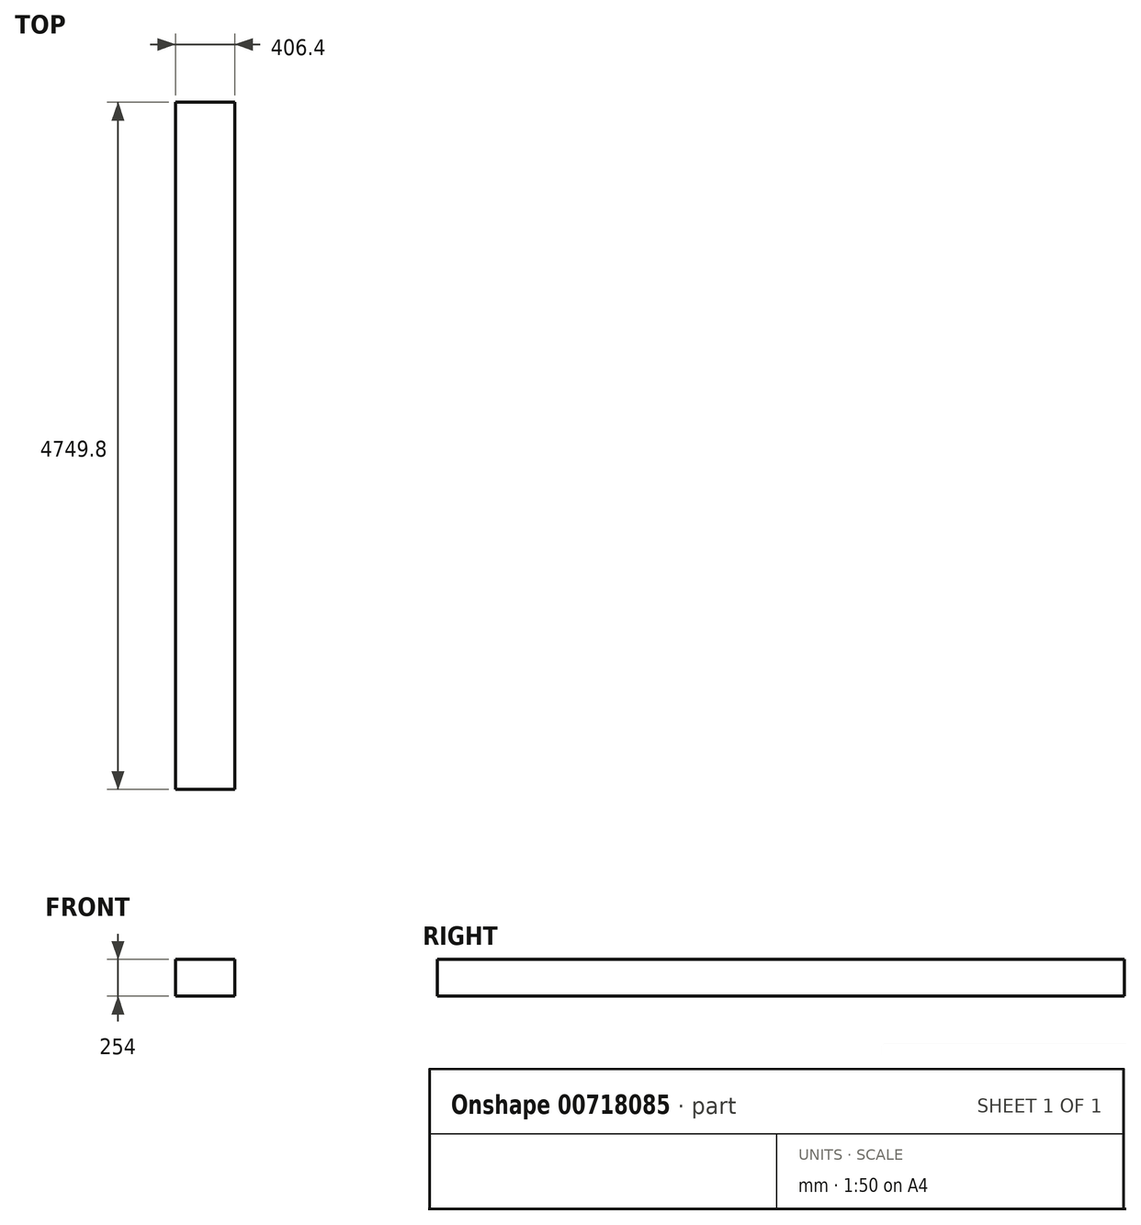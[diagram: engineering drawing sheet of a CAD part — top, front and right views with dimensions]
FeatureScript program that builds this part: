
annotation { "Feature Type Name" : "Feature", "Feature Type Description" : "" }
export const myFeature = defineFeature(function(context is Context, id is Id, definition is map)
    precondition{}
    {
        {
            var Q0;
            Q0=qCreatedBy(makeId("Front.planeOp"),FACE);
            var sketch = newSketch(context, id + "F0", { "sketchPlane" : qUnion([Q0])});
            skLineSegment(sketch, "E0.bottom", {"start": v(203.2, -127) * mm, "end": v(-203.2, -127) * mm});
            skLineSegment(sketch, "E0.top", {"start": v(203.2, 127) * mm, "end": v(-203.2, 127) * mm});
            skLineSegment(sketch, "E0.left", {"start": v(203.2, -127) * mm, "end": v(203.2, 127) * mm});
            skLineSegment(sketch, "E0.right", {"start": v(-203.2, -127) * mm, "end": v(-203.2, 127) * mm});
            skPoint(sketch, "E0.middle", {"position": v(0, 0) * mm});
            skSolve(sketch);
        }
        {
            var Q0;
            Q0=qSketchRegion(id+"F0",true);
            extrude(context, id + "F1", {"entities" : qUnion([Q0]), "depth" : 4749.8 * mm, "offsetDistance" : 25.4 * mm});
        }
    });
